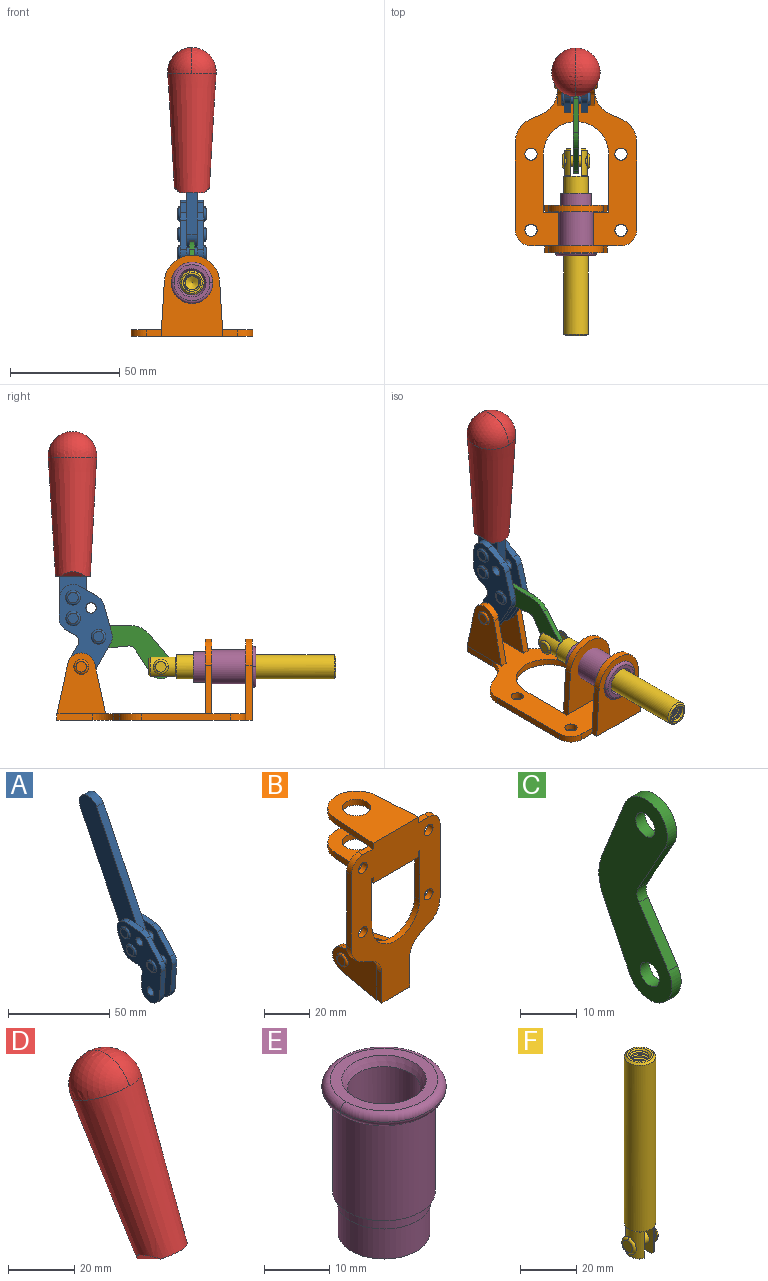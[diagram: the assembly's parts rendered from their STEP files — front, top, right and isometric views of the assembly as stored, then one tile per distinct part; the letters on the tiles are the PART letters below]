
ASSEMBLY  parts=6 mates=6
PART A: 59 faces, bbox 12.9x60.2x99.6 mm
  f0: torus R=2.39mm, axis (-1,0,0), area 14.9mm2, adj f20,f43,f51
  f1: torus R=2.39mm, axis (-1,0,0), area 14.9mm2, adj f19,f42,f51
  f2: torus R=2.39mm, axis (-1,0,0), area 14.9mm2, adj f18,f35,f51
  f3: torus R=2.39mm, axis (-1,0,0), area 14.9mm2, adj f14,f17,f23
  f4: torus R=2.39mm, axis (-1,0,0), area 14.9mm2, adj f13,f16,f23
  f5: torus R=2.39mm, axis (-1,0,0), area 14.9mm2, adj f12,f15,f23
  f6: cylinder r=2.39mm len=4.78mm, axis (1,0,0), area 46.5mm2, adj f48,f50,f51
  f7: cylinder r=2.39mm len=4.78mm, axis (1,0,0), area 46.5mm2, adj f50,f51
  f8: cylinder r=6.35mm len=12.68mm, axis (1,0,0), area 61.8mm2, adj f38,f39,f50,f51
  f9: cylinder r=2.39mm len=4.78mm, axis (-1,0,0), area 70.5mm2, adj f46,f50
  f10: cylinder r=2.39mm len=4.78mm, axis (-1,0,0), area 46.5mm2, adj f23,f45,f46
  f11: cylinder r=2.39mm len=4.78mm, axis (-1,0,0), area 46.5mm2, adj f23,f46
  f12: plane 4.78x4.78mm, normal (1,0,0), area 17.9mm2, adj f5,f15
  f13: plane 4.78x4.78mm, normal (1,0,0), area 17.9mm2, adj f4,f16
  f14: plane 4.78x4.78mm, normal (1,0,0), area 17.9mm2, adj f3,f17
  f15: torus R=2.39mm, axis (-1,0,0), area 14.9mm2, adj f5,f12,f23
  f16: torus R=2.39mm, axis (-1,0,0), area 14.9mm2, adj f4,f13,f23
  f17: torus R=2.39mm, axis (-1,0,0), area 14.9mm2, adj f3,f14,f23
  f18: plane 4.78x4.78mm, normal (-1,0,0), area 17.9mm2, adj f2,f35
  f19: plane 4.78x4.78mm, normal (-1,0,0), area 17.9mm2, adj f1,f42
  f20: plane 4.78x4.78mm, normal (-1,0,0), area 17.9mm2, adj f0,f43
  f21: plane 2.26x0.2mm, normal (1,0,0), area 0.2mm2, adj f31,f44
  f22: plane 2.26x0.2mm, normal (-1,0,0), area 0.2mm2, adj f41,f44
  f23: plane 39.37x30.77mm, normal (1,0,0), area 565.5mm2, adj f3,f4,f5,f10,f11,f15,f16,f17
  f24: cylinder r=6.1mm len=4.15mm, axis (-1,0,0), area 14.7mm2, adj f23,f25,f32,f46
  f25: plane 10.25x9.01mm, normal (0,-0.75,0.66), area 42.3mm2, adj f23,f24,f26,f46
  f26: cylinder r=6.35mm len=4.64mm, axis (-1,0,0), area 15.6mm2, adj f23,f25,f27,f46
  f27: plane 15.84x3.1mm, normal (0,-1,-0.07), area 49.2mm2, adj f23,f26,f28,f46
  f28: cylinder r=6.35mm len=12.68mm, axis (-1,0,0), area 61.8mm2, adj f23,f27,f29,f46
  f29: plane 8.11x3.1mm, normal (0,1,0.07), area 25.2mm2, adj f23,f28,f30,f46
  f30: cylinder r=3.05mm len=3.25mm, axis (-1,0,0), area 14.8mm2, adj f23,f29,f31,f46
  f31: plane 5.99x3.1mm, normal (0,0.07,-1), area 18.6mm2, adj f21,f23,f30,f44,f46
  f32: plane 9.5x3.1mm, normal (0,-0.07,1), area 29.5mm2, adj f23,f24,f33,f46,f47
  f33: cylinder r=6.1mm len=8.63mm, axis (-1,0,0), area 39.1mm2, adj f23,f32,f34,f47
  f34: plane 8.65x3.96mm, normal (0,0.91,-0.42), area 29.5mm2, adj f23,f33,f44,f47
  f35: torus R=2.39mm, axis (-1,0,0), area 14.9mm2, adj f2,f18,f51
  f36: plane 10.25x9.01mm, normal (0,-0.75,0.66), area 42.3mm2, adj f37,f49,f50,f51
  f37: cylinder r=6.35mm len=4.64mm, axis (1,0,0), area 15.6mm2, adj f36,f38,f50,f51
  f38: plane 15.84x3.1mm, normal (0,-1,-0.07), area 49.2mm2, adj f8,f37,f50,f51
  f39: plane 8.11x3.1mm, normal (0,1,0.07), area 25.2mm2, adj f8,f40,f50,f51
  f40: cylinder r=3.05mm len=3.25mm, axis (1,0,0), area 14.8mm2, adj f39,f41,f50,f51
  f41: plane 5.99x3.1mm, normal (0,0.07,-1), area 18.6mm2, adj f22,f40,f44,f50,f51
  f42: torus R=2.39mm, axis (-1,0,0), area 14.9mm2, adj f1,f19,f51
  f43: torus R=2.39mm, axis (-1,0,0), area 14.9mm2, adj f0,f20,f51
  f44: cylinder r=6.35mm len=12.12mm, axis (-1,0,0), area 128.9mm2, adj f21,f22,f23,f31,f34,f41,f46,f47
  f45: plane 2.65x1.35mm, normal (1,0,0), area 1mm2, adj f10,f55
  f46: plane 39.08x20.42mm, normal (-1,0,0), area 412.5mm2, adj f9,f10,f11,f24,f25,f26,f27,f28
  f47: plane 77.62x39.82mm, normal (1,0,0), area 850mm2, adj f32,f33,f34,f44,f53,f54,f55
  f48: plane 2.65x1.35mm, normal (-1,0,0), area 1mm2, adj f6,f55
  f49: cylinder r=6.1mm len=4.15mm, axis (1,0,0), area 14.7mm2, adj f36,f50,f51,f56
  f50: plane 39.08x20.42mm, normal (1,0,0), area 412.5mm2, adj f6,f7,f8,f9,f36,f37,f38,f39
  f51: plane 39.37x30.77mm, normal (-1,0,0), area 565.5mm2, adj f0,f1,f2,f6,f7,f8,f35,f36
  f52: plane 8.65x3.96mm, normal (0,0.91,-0.42), area 29.5mm2, adj f44,f51,f57,f58
  f53: plane 68.49x33.4mm, normal (0,0.9,-0.44), area 358.1mm2, adj f44,f47,f54,f58
  f54: cylinder r=6.35mm len=12.06mm, axis (1,0,0), area 93.7mm2, adj f47,f53,f55,f58
  f55: plane 68.49x33.4mm, normal (0,-0.9,0.44), area 358.1mm2, adj f44,f45,f46,f47,f48,f50,f54,f58
  f56: plane 9.5x3.1mm, normal (0,-0.07,1), area 29.5mm2, adj f49,f50,f51,f57,f58
  f57: cylinder r=6.1mm len=8.63mm, axis (1,0,0), area 39.1mm2, adj f51,f52,f56,f58
  f58: plane 77.62x39.82mm, normal (-1,0,0), area 850mm2, adj f44,f52,f53,f54,f55,f56,f57
PART B: 55 faces, bbox 55.7x37.4x89.8 mm
  f0: torus R=2.41mm, axis (-1,0,0), area 15mm2, adj f11,f15,f25
  f1: torus R=2.41mm, axis (-1,0,0), area 15mm2, adj f10,f12,f22
  f2: cylinder r=2.78mm len=5.56mm, axis (0,-1,0), area 54.2mm2, adj f30,f54
  f3: cylinder r=14.99mm len=29.97mm, axis (0,-1,0), area 145.9mm2, adj f30,f49,f53,f54
  f4: cylinder r=2.78mm len=5.56mm, axis (0,-1,0), area 54.2mm2, adj f30,f54
  f5: cylinder r=2.78mm len=5.56mm, axis (0,-1,0), area 54.2mm2, adj f30,f54
  f6: cylinder r=2.78mm len=5.56mm, axis (0,-1,0), area 54.2mm2, adj f30,f54
  f7: cylinder r=6.35mm len=12.7mm, axis (0,0,1), area 123.6mm2, adj f27,f51
  f8: cylinder r=6.35mm len=12.7mm, axis (0,0,-1), area 124.7mm2, adj f21,f35
  f9: cylinder r=2.41mm len=11.18mm, axis (-1,0,0), area 169.4mm2, adj f16,f19
  f10: plane 4.83x4.83mm, normal (1,0,0), area 18.3mm2, adj f1,f12
  f11: plane 4.83x4.83mm, normal (-1,0,0), area 18.3mm2, adj f0,f15
  f12: torus R=2.41mm, axis (-1,0,0), area 15mm2, adj f1,f10,f22
  f13: cylinder r=6.35mm len=12.41mm, axis (1,0,0), area 53.4mm2, adj f18,f19,f22,f23
  f14: cylinder r=6.35mm len=12.41mm, axis (-1,0,0), area 53.4mm2, adj f16,f17,f24,f25
  f15: torus R=2.41mm, axis (-1,0,0), area 15mm2, adj f0,f11,f25
  f16: plane 27.86x22.35mm, normal (1,0,0), area 425.4mm2, adj f9,f14,f17,f24,f30
  f17: plane 22.86x4.97mm, normal (0,0.21,0.98), area 72.5mm2, adj f14,f16,f25,f30
  f18: plane 22.86x4.97mm, normal (0,0.21,0.98), area 72.5mm2, adj f13,f19,f22,f30
  f19: plane 27.86x22.35mm, normal (-1,0,0), area 425.4mm2, adj f9,f13,f18,f23,f30
  f20: cylinder r=12.7mm len=25.35mm, axis (0,0,-1), area 119.8mm2, adj f21,f34,f35,f36
  f21: plane 34.21x28.07mm, normal (0,0,-1), area 702.4mm2, adj f8,f20,f30,f34,f36
  f22: plane 27.96x22.45mm, normal (1,0,0), area 407.2mm2, adj f1,f12,f13,f18,f23,f30,f42,f43
  f23: plane 22.86x4.97mm, normal (0,0.21,-0.98), area 72.5mm2, adj f13,f19,f22,f44
  f24: plane 22.86x4.97mm, normal (0,0.21,-0.98), area 72.5mm2, adj f14,f16,f25,f44
  f25: plane 27.86x22.35mm, normal (-1,0,0), area 407.1mm2, adj f0,f14,f15,f17,f24,f30,f45,f46
  f26: plane 3.1x0.95mm, normal (0,0,-1), area 2.7mm2, adj f30,f49,f50,f54
  f27: plane 34.21x28.07mm, normal (0,0,1), area 702.4mm2, adj f7,f28,f30,f50,f52
  f28: cylinder r=12.7mm len=25.35mm, axis (0,0,1), area 118.8mm2, adj f27,f50,f51,f52
  f29: plane 3.1x0.95mm, normal (0,0,-1), area 2.7mm2, adj f30,f52,f53,f54
  f30: plane 86.54x55.63mm, normal (0,1,0), area 2362.9mm2, adj f2,f3,f4,f5,f6,f16,f17,f18
  f31: plane 40.56x3.1mm, normal (-1,0,0), area 125.7mm2, adj f30,f32,f48,f54
  f32: cylinder r=7.11mm len=7.11mm, axis (0,-1,0), area 34.6mm2, adj f30,f31,f33,f54
  f33: plane 6.67x3.1mm, normal (0,0,1), area 20.4mm2, adj f30,f32,f34,f54
  f34: plane 25.39x3.13mm, normal (-1,0.06,0), area 79.5mm2, adj f20,f21,f33,f35,f54
  f35: plane 37.31x28.45mm, normal (0,0,1), area 789.9mm2, adj f8,f20,f34,f36,f54
  f36: plane 25.39x3.13mm, normal (1,0.06,0), area 79.5mm2, adj f20,f21,f35,f37,f54
  f37: plane 6.67x3.1mm, normal (0,0,1), area 20.4mm2, adj f30,f36,f38,f54
  f38: cylinder r=7.11mm len=7.11mm, axis (0,-1,0), area 34.6mm2, adj f30,f37,f39,f54
  f39: plane 40.56x3.1mm, normal (1,0,0), area 125.7mm2, adj f30,f38,f40,f54
  f40: cylinder r=11.18mm len=10.16mm, axis (0,-1,0), area 39.5mm2, adj f30,f39,f41,f54
  f41: plane 6.09x3.1mm, normal (0.42,0,-0.91), area 20.8mm2, adj f30,f40,f42,f54
  f42: cylinder r=11.18mm len=9.41mm, axis (0,-1,0), area 37.2mm2, adj f22,f30,f41,f43,f54
  f43: plane 16.5x3.1mm, normal (1,0,0), area 51.1mm2, adj f22,f42,f44,f54
  f44: plane 17.37x3.1mm, normal (0,0,-1), area 53.8mm2, adj f23,f24,f30,f43,f45,f54
  f45: plane 16.5x3.1mm, normal (-1,0,0), area 51.1mm2, adj f25,f44,f46,f54
  f46: cylinder r=11.18mm len=9.41mm, axis (0,-1,0), area 37.2mm2, adj f25,f30,f45,f47,f54
  f47: plane 6.09x3.1mm, normal (-0.42,0,-0.91), area 20.8mm2, adj f30,f46,f48,f54
  f48: cylinder r=11.18mm len=10.16mm, axis (0,-1,0), area 39.5mm2, adj f30,f31,f47,f54
  f49: plane 26.54x3.1mm, normal (-1,0,0), area 82.3mm2, adj f3,f26,f30,f54
  f50: plane 25.39x3.1mm, normal (1,0.06,0), area 78.8mm2, adj f26,f27,f28,f51,f54
  f51: plane 37.31x28.45mm, normal (0,0,-1), area 789.9mm2, adj f7,f28,f50,f52,f54
  f52: plane 25.39x3.1mm, normal (-1,0.06,0), area 78.8mm2, adj f27,f28,f29,f51,f54
  f53: plane 26.54x3.1mm, normal (1,0,0), area 82.3mm2, adj f3,f29,f30,f54
  f54: plane 89.66x55.63mm, normal (0,-1,0), area 2678.5mm2, adj f2,f3,f4,f5,f6,f26,f29,f31
PART C: 12 faces, bbox 2.3x18.2x42.8 mm
  f0: cylinder r=2.4mm len=4.8mm, axis (1,0,0), area 34.9mm2, adj f4,f11
  f1: cylinder r=10.41mm len=8.47mm, axis (1,0,0), area 20.2mm2, adj f4,f9,f10,f11
  f2: cylinder r=3.05mm len=3.16mm, axis (1,0,0), area 7.7mm2, adj f4,f6,f7,f11
  f3: cylinder r=2.4mm len=4.8mm, axis (1,0,0), area 34.9mm2, adj f4,f11
  f4: plane 42.81x18.23mm, normal (-1,0,0), area 414.1mm2, adj f0,f1,f2,f3,f5,f6,f7,f8
  f5: cylinder r=5.54mm len=10.67mm, axis (1,0,0), area 41.8mm2, adj f4,f6,f10,f11
  f6: plane 11.66x6.53mm, normal (0,-0.87,-0.49), area 30.9mm2, adj f2,f4,f5,f11
  f7: plane 11.17x7.33mm, normal (0,-0.84,0.55), area 30.9mm2, adj f2,f4,f8,f11
  f8: cylinder r=5.54mm len=10.51mm, axis (1,0,0), area 41.8mm2, adj f4,f7,f9,f11
  f9: plane 13.67x6.67mm, normal (0,0.9,-0.44), area 35.1mm2, adj f1,f4,f8,f11
  f10: plane 14.1x5.7mm, normal (0,0.93,0.37), area 35.1mm2, adj f1,f4,f5,f11
  f11: plane 42.81x18.23mm, normal (1,0,0), area 414.1mm2, adj f0,f1,f2,f3,f5,f6,f7,f8
PART D: 11 faces, bbox 22.3x42.6x64.5 mm
  f0: sphere r=11.13mm, area 411.4mm2, adj f1,f8
  f1: cone r=11.11mm half-angle=3.3deg, axis (0,0.44,0.9), area 3251.8mm2, adj f0,f7,f8,f9,f10
  f2: cylinder r=6.16mm len=11.7mm, axis (1,0,0), area 89.5mm2, adj f3,f4,f5,f6
  f3: plane 60.23x36.75mm, normal (-1,0,0), area 763.6mm2, adj f2,f4,f6,f10
  f4: plane 51.37x25.05mm, normal (0,0.9,-0.44), area 264.2mm2, adj f2,f3,f5,f10
  f5: plane 60.23x36.75mm, normal (1,0,0), area 763.6mm2, adj f2,f4,f6,f10
  f6: plane 51.37x25.05mm, normal (0,-0.9,0.44), area 264.2mm2, adj f2,f3,f5,f10
  f7: plane 9.95x5.95mm, normal (0.71,-0.31,-0.64), area 25.8mm2, adj f1,f10
  f8: sphere r=11.13mm, area 411.4mm2, adj f0,f1
  f9: plane 9.95x5.95mm, normal (-0.71,-0.31,-0.64), area 25.8mm2, adj f1,f10
  f10: plane 14.27x11.38mm, normal (0,-0.44,-0.9), area 106.7mm2, adj f1,f3,f4,f5,f6,f7,f9
PART E: 15 faces, bbox 20.6x20.6x28.7 mm
  f0: torus R=8.26mm, axis (0,0,1), area 56.8mm2, adj f1,f10,f12
  f1: torus R=8.26mm, axis (0,0,1), area 56.8mm2, adj f0,f6,f13
  f2: cylinder r=5.59mm len=25.91mm, axis (0,0,1), area 909.6mm2, adj f3,f4
  f3: cone r=6.86mm half-angle=45deg, axis (0,0,-1), area 70.2mm2, adj f2,f14
  f4: cone r=6.47mm half-angle=30deg, axis (0,0,1), area 66.7mm2, adj f2,f13
  f5: cylinder r=7.04mm len=14.07mm, axis (0,0,1), area 252.6mm2, adj f11,f14
  f6: torus R=8.26mm, axis (0,0,1), area 56.8mm2, adj f1,f12,f13
  f7: cylinder r=7.16mm len=14.33mm, axis (0,0,1), area 91.5mm2, adj f9,f11
  f8: cylinder r=7.86mm len=18.42mm, axis (0,0,1), area 909.6mm2, adj f9,f10
  f9: plane 15.72x15.72mm, normal (0,0,-1), area 33mm2, adj f7,f8
  f10: plane 16.51x16.51mm, normal (0,0,-1), area 19.9mm2, adj f0,f8,f12
  f11: plane 14.33x14.33mm, normal (0,0,-1), area 5.7mm2, adj f5,f7
  f12: torus R=8.26mm, axis (0,0,1), area 56.8mm2, adj f0,f6,f10
  f13: plane 16.51x16.51mm, normal (0,0,1), area 82.7mm2, adj f1,f4,f6
  f14: plane 14.07x14.07mm, normal (0,0,-1), area 7.8mm2, adj f3,f5
PART F: 48 faces, bbox 12.6x11.1x86.1 mm
  f0: torus R=2.41mm, axis (-1,0,0), area 15mm2, adj f30,f32,f34
  f1: torus R=2.41mm, axis (-1,0,0), area 15mm2, adj f29,f31,f33
  f2: cylinder r=5.54mm len=72.39mm, axis (0,0,1), area 2518.5mm2, adj f3,f4,f42,f43
  f3: cone r=5.54mm half-angle=45deg, axis (0,0,1), area 7.6mm2, adj f2,f5,f41
  f4: cone r=5.54mm half-angle=45deg, axis (0,0,-1), area 34.9mm2, adj f2,f39
  f5: cylinder r=5.08mm len=11.48mm, axis (0,0,1), area 108.3mm2, adj f3,f7,f8,f41
  f6: cylinder r=2.41mm len=4.83mm, axis (-1,0,0), area 71.2mm2, adj f40,f41
  f7: cylinder r=2.41mm len=4.83mm, axis (-1,0,0), area 7.6mm2, adj f5,f34
  f8: cone r=5.08mm half-angle=45deg, axis (0,0,1), area 10.6mm2, adj f5,f37,f41
  f9: cone r=3.98mm half-angle=45deg, axis (0,0,1), area 17.6mm2, adj f27,f39,f45,f46,f47
  f10: cylinder r=2.41mm len=4.83mm, axis (-1,0,0), area 7.6mm2, adj f33,f38
  f11: cylinder r=3.2mm len=6.4mm, axis (0,0,1), area 78.4mm2, adj f12,f28,f44,f45,f47
  f12: cylinder r=3.2mm len=6.4mm, axis (0,0,1), area 10.5mm2, adj f11,f13,f45,f47
  f13: cylinder r=3.2mm len=6.4mm, axis (0,0,1), area 10.5mm2, adj f12,f14,f45,f47
  f14: cylinder r=3.2mm len=6.4mm, axis (0,0,1), area 10.5mm2, adj f13,f15,f45,f47
  f15: cylinder r=3.2mm len=6.4mm, axis (0,0,1), area 10.5mm2, adj f14,f16,f45,f47
  f16: cylinder r=3.2mm len=6.4mm, axis (0,0,1), area 10.5mm2, adj f15,f17,f45,f47
  f17: cylinder r=3.2mm len=6.4mm, axis (0,0,1), area 10.5mm2, adj f16,f18,f45,f47
  f18: cylinder r=3.2mm len=6.4mm, axis (0,0,1), area 10.5mm2, adj f17,f19,f45,f47
  f19: cylinder r=3.2mm len=6.4mm, axis (0,0,1), area 10.5mm2, adj f18,f20,f45,f47
  f20: cylinder r=3.2mm len=6.4mm, axis (0,0,1), area 10.5mm2, adj f19,f21,f45,f47
  f21: cylinder r=3.2mm len=6.4mm, axis (0,0,1), area 10.5mm2, adj f20,f22,f45,f47
  f22: cylinder r=3.2mm len=6.4mm, axis (0,0,1), area 10.5mm2, adj f21,f23,f45,f47
  f23: cylinder r=3.2mm len=6.4mm, axis (0,0,1), area 10.5mm2, adj f22,f24,f45,f47
  f24: cylinder r=3.2mm len=6.4mm, axis (0,0,1), area 10.5mm2, adj f23,f25,f45,f47
  f25: cylinder r=3.2mm len=6.4mm, axis (0,0,1), area 10.5mm2, adj f24,f26,f45,f47
  f26: cylinder r=3.2mm len=6.4mm, axis (0,0,1), area 10.5mm2, adj f25,f27,f45,f47
  f27: cylinder r=3.2mm len=6.4mm, axis (0,0,1), area 7.4mm2, adj f9,f26,f45,f47
  f28: cone r=3.2mm half-angle=60deg, axis (0,0,1), area 37.2mm2, adj f11
  f29: plane 4.83x4.83mm, normal (-1,0,0), area 18.3mm2, adj f1,f31
  f30: plane 4.83x4.83mm, normal (1,0,0), area 18.3mm2, adj f0,f32
  f31: torus R=2.41mm, axis (-1,0,0), area 15mm2, adj f1,f29,f33
  f32: torus R=2.41mm, axis (-1,0,0), area 15mm2, adj f0,f30,f34
  f33: plane 6.83x6.83mm, normal (1,0,0), area 18.3mm2, adj f1,f10,f31
  f34: plane 6.83x6.83mm, normal (-1,0,0), area 18.3mm2, adj f0,f7,f32
  f35: cone r=5.08mm half-angle=45deg, axis (0,0,1), area 10.6mm2, adj f36,f38,f40
  f36: plane 7.25x1.97mm, normal (0,0,-1), area 10mm2, adj f35,f40
  f37: plane 7.25x1.97mm, normal (0,0,-1), area 10mm2, adj f8,f41
  f38: cylinder r=5.08mm len=11.48mm, axis (0,0,1), area 108.3mm2, adj f10,f35,f40,f42
  f39: plane 9.55x9.55mm, normal (0,0,1), area 22mm2, adj f4,f9
  f40: plane 12.76x10.09mm, normal (1,0,0), area 95.7mm2, adj f6,f35,f36,f38,f42,f43
  f41: plane 12.76x10.09mm, normal (-1,0,0), area 95.7mm2, adj f3,f5,f6,f8,f37,f43
  f42: cone r=5.54mm half-angle=45deg, axis (0,0,1), area 7.6mm2, adj f2,f38,f40
  f43: plane 11.07x4.7mm, normal (0,0,-1), area 50.4mm2, adj f2,f40,f41
  f44: plane 0.89x0.62mm, normal (-1,0,0), area 0.3mm2, adj f11,f45,f46,f47
  f45: bspline ~24.8x7.63mm, area 266.6mm2, adj f9,f11,f12,f13,f14,f15,f16,f17
  f46: bspline ~24.87x7.63mm, area 73.6mm2, adj f9,f44,f45,f47
  f47: bspline ~24.98x7.63mm, area 272.5mm2, adj f9,f11,f12,f13,f14,f15,f16,f17
PLACE A rot(axis=(1,0,0),25.8deg) t=(0,-2.46,24.16)mm
PLACE B rot(axis=(1,0,0),90deg) t=(0,1.56,-18.66)mm fixed
PLACE C rot(axis=(1,0,0),117.7deg) t=(0,22.32,-8.63)mm
PLACE D rot(axis=(1,0,0),25.8deg) t=(-0.04,-2.46,24.16)mm
PLACE E rot(axis=(1,0,0),90deg) t=(0,2.58,-18.66)mm
PLACE F rot(axis=(1,0,0),90deg) t=(0,12.65,-18.66)mm
MATE slider B.f7 <-> F.f2  axis (0,-1,0) through (0,-44.83,5.96)mm
MATE revolute A.f7 <-> B.f0  axis (1,0,0) through (0,33.65,5.96)mm
MATE fastened D.f2 <-> A.f54  axis (1,0,0) through (-2.35,37.72,104.37)mm
MATE revolute C.f5 <-> F.f6  axis (1,0,0) through (0,-2.83,5.96)mm
MATE fastened B.f7 <-> E.f2  axis (0,1,0) through (0,-44.83,5.96)mm
MATE revolute C.f3 <-> A.f4  axis (1,0,0) through (0,25.77,19.74)mm
